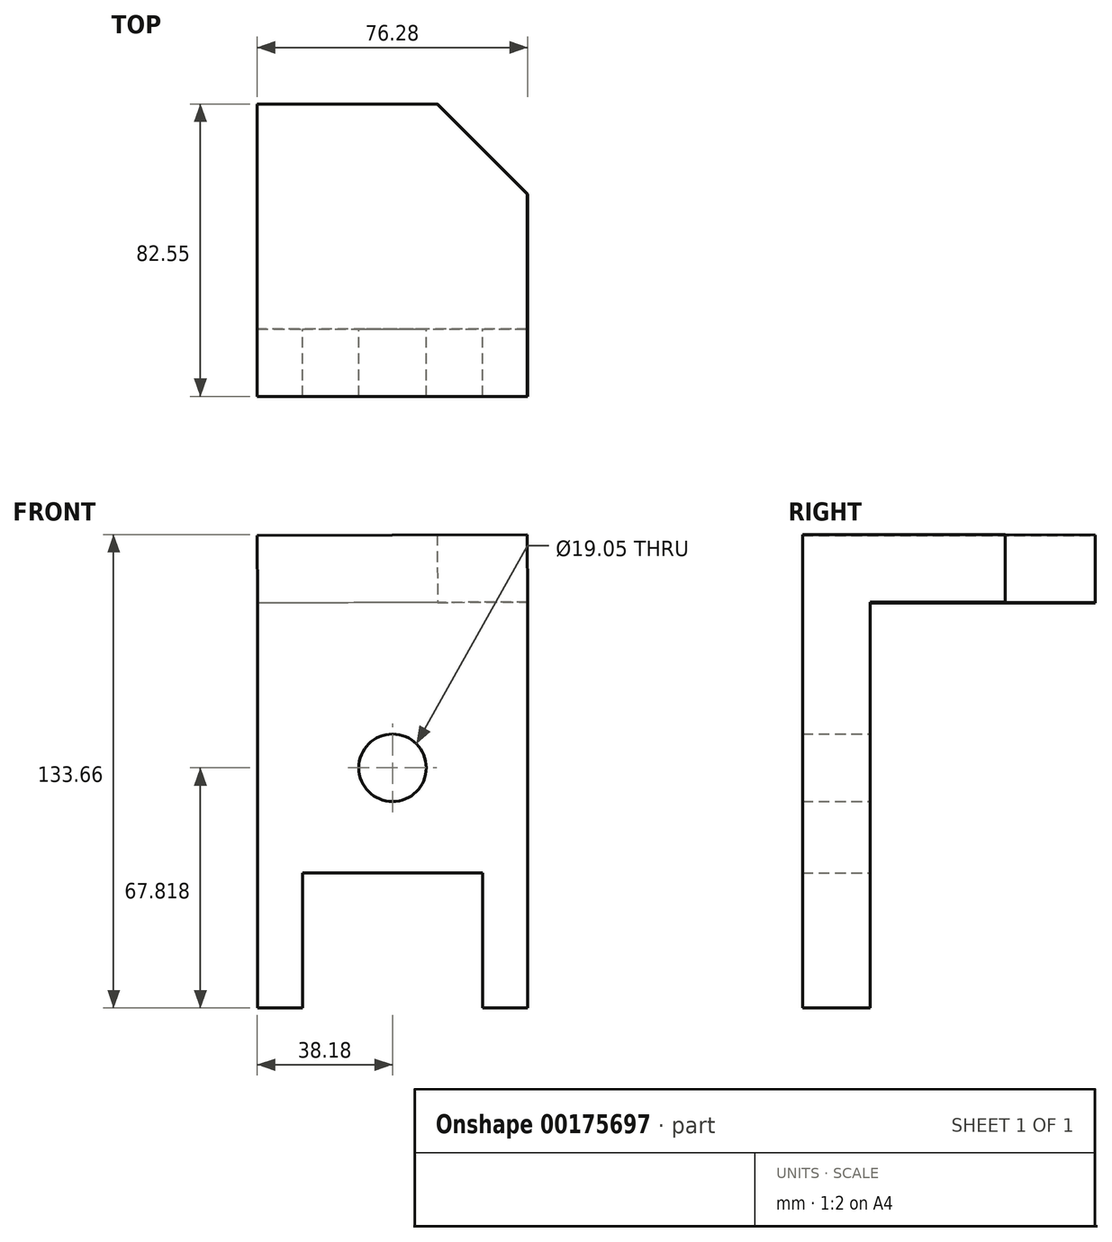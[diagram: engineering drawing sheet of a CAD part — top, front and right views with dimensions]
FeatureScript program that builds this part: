
annotation { "Feature Type Name" : "Feature", "Feature Type Description" : "" }
export const myFeature = defineFeature(function(context is Context, id is Id, definition is map)
    precondition{}
    {
        {
            var Q0;
            Q0=qCreatedBy(makeId("Front.planeOp"),FACE);
            var sketch = newSketch(context, id + "F0", { "sketchPlane" : qUnion([Q0])});
            skLineSegment(sketch, "E0", {"start": v(-18.85, 76.2) * mm, "end": v(-18.85, -38.1) * mm});
            skLineSegment(sketch, "E1", {"start": v(-18.85, -38.1) * mm, "end": v(-6.15, -38.1) * mm});
            skLineSegment(sketch, "E2", {"start": v(-6.15, -38.1) * mm, "end": v(-6.15, 0) * mm});
            skLineSegment(sketch, "E3", {"start": v(-6.15, 0) * mm, "end": v(44.65, 0) * mm});
            skLineSegment(sketch, "E4", {"start": v(44.65, 0) * mm, "end": v(44.65, -38.1) * mm});
            skLineSegment(sketch, "E5", {"start": v(44.65, -38.1) * mm, "end": v(57.35, -38.1) * mm});
            skLineSegment(sketch, "E6", {"start": v(57.35, -38.1) * mm, "end": v(57.35, 0) * mm});
            skLineSegment(sketch, "E7", {"start": v(57.35, 0) * mm, "end": v(57.35, 76.5) * mm});
            skLineSegment(sketch, "E8", {"start": v(57.35, 76.5) * mm, "end": v(-18.85, 76.2) * mm});
            skCircle(sketch, "E9", {"center": v(19.25, 29.72) * mm, "radius": 9.53 * mm});
            skSolve(sketch);
        }
        {
            var Q0;
            Q0=makeQuery(id+"F0.imprint","IMPRINT",FACE,{"disambiguationData":[TD([[makeQuery(id+"F0.imprint","IMPRINT",EDGE,{"derivedFrom":sQuery(id+"F0.wireOp",EDGE,"E0")}),1.0]])]});
            extrude(context, id + "F1", {"entities" : qUnion([Q0]), "depth" : 19.05 * mm});
        }
        {
            var Q0;
            Q0=makeQuery(id+"F1.opExtrude","SWEPT_FACE",FACE,{"disambiguationData":[OSD([sQuery(id+"F0.wireOp",EDGE,"E8")])]});
            var sketch = newSketch(context, id + "F2", { "sketchPlane" : qUnion([Q0])});
            skLineSegment(sketch, "E10", {"start": v(57.66, 0) * mm, "end": v(57.66, 38.1) * mm});
            skLineSegment(sketch, "E11", {"start": v(-18.54, 0) * mm, "end": v(-18.54, 63.5) * mm});
            skLineSegment(sketch, "E12", {"start": v(32.26, 63.5) * mm, "end": v(-18.54, 63.5) * mm});
            skLineSegment(sketch, "E13", {"start": v(32.26, 63.5) * mm, "end": v(57.66, 38.1) * mm});
            skSolve(sketch);
        }
        {
            var Q0;
            Q0=makeQuery(id+"F2.imprint","IMPRINT",FACE,{"disambiguationData":[TD([[makeQuery(id+"F2.imprint","IMPRINT",EDGE,{"derivedFrom":sQuery(id+"F2.wireOp",EDGE,"E10")}),1.0]])]});
            var Q1;
            {var subQ0=sQuery(id+"F0.wireOp",EDGE,"E8");Q1=makeQuery(id+"F2.imprint","IMPRINT",FACE,{"disambiguationData":[TD([[makeQuery(id+"F2.imprint","IMPRINT",EDGE,{"derivedFrom":makeQuery(id+"F1.opExtrude","CAP_EDGE",EDGE,{"disambiguationData":[OSD([subQ0])],"isStart":true})}),1.0]])]});}
            extrude(context, id + "F3", {"entities" : qUnion([Q0, Q1]), "operationType" : NewBodyOperationType.ADD, "depth" : 19.05 * mm});
        }
    });
